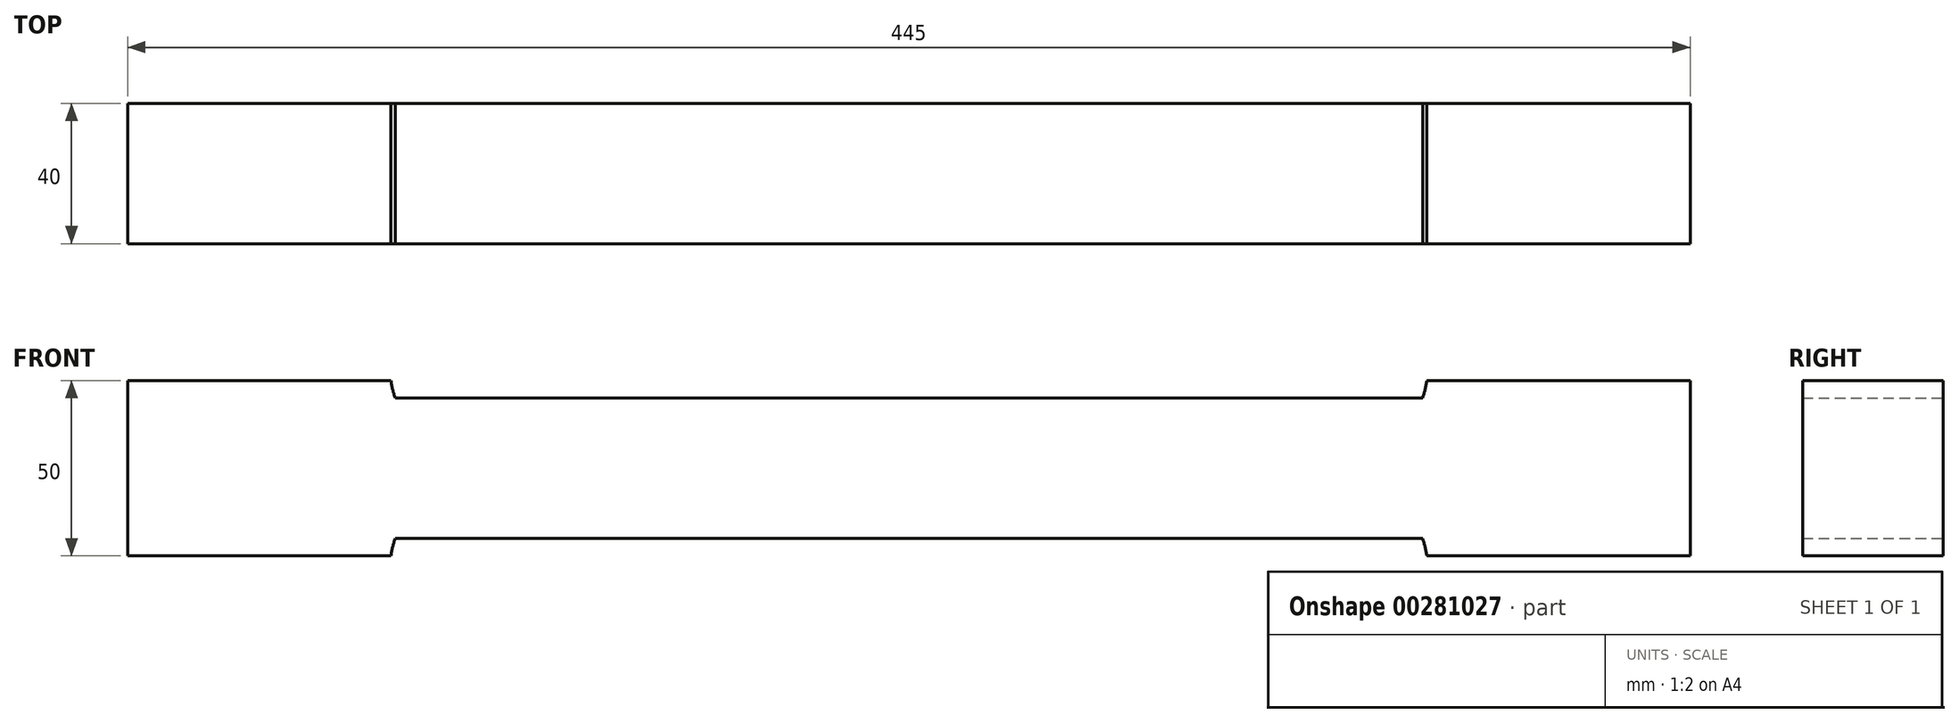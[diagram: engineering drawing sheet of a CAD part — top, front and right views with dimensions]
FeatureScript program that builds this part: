
annotation { "Feature Type Name" : "Feature", "Feature Type Description" : "" }
export const myFeature = defineFeature(function(context is Context, id is Id, definition is map)
    precondition{}
    {
        {
            var Q0;
            Q0=qCreatedBy(makeId("Front.planeOp"),FACE);
            var sketch = newSketch(context, id + "F0", { "sketchPlane" : qUnion([Q0])});
            skLineSegment(sketch, "E0", {"start": v(0, 20) * mm, "end": v(146.3, 20) * mm});
            skArc(sketch, "E1", {"start": v(146.3, 20) * mm, "mid": v(147.03, 22.47) * mm, "end": v(147.5, 25) * mm});
            skLineSegment(sketch, "E2", {"start": v(147.5, 25) * mm, "end": v(222.5, 25) * mm});
            skLineSegment(sketch, "E3", {"start": v(222.5, 25) * mm, "end": v(222.5, 0) * mm});
            skLineSegment(sketch, "E4.MirrorCS", {"start": v(0, -20) * mm, "end": v(146.3, -20) * mm});
            skLineSegment(sketch, "E5.MirrorCS", {"start": v(222.5, -25) * mm, "end": v(222.5, 0) * mm});
            skLineSegment(sketch, "E6.MirrorCS", {"start": v(147.5, -25) * mm, "end": v(222.5, -25) * mm});
            skArc(sketch, "E7.MirrorCS", {"start": v(146.3, -20) * mm, "mid": v(147.03, -22.47) * mm, "end": v(147.5, -25) * mm});
            skLineSegment(sketch, "E8.MirrorCS", {"start": v(0, -20) * mm, "end": v(-146.3, -20) * mm});
            skLineSegment(sketch, "E9.MirrorCS", {"start": v(-222.5, -25) * mm, "end": v(-222.5, 0) * mm});
            skArc(sketch, "E10.MirrorCS", {"start": v(-146.3, -20) * mm, "mid": v(-147.03, -22.47) * mm, "end": v(-147.5, -25) * mm});
            skLineSegment(sketch, "E11.MirrorCS", {"start": v(-147.5, -25) * mm, "end": v(-222.5, -25) * mm});
            skArc(sketch, "E12.MirrorCS", {"start": v(-146.3, 20) * mm, "mid": v(-147.03, 22.47) * mm, "end": v(-147.5, 25) * mm});
            skLineSegment(sketch, "E13.MirrorCS", {"start": v(-147.5, 25) * mm, "end": v(-222.5, 25) * mm});
            skLineSegment(sketch, "E14.MirrorCS", {"start": v(-222.5, 25) * mm, "end": v(-222.5, 0) * mm});
            skLineSegment(sketch, "E15.MirrorCS", {"start": v(0, 20) * mm, "end": v(-146.3, 20) * mm});
            skSolve(sketch);
        }
        {
            var Q0;
            Q0 = qSketchRegion(id + "F0", true);
            extrude(context, id + "F1", {"entities" : qUnion([Q0]), "endBound" : BoundingType.SYMMETRIC, "depth" : 40 * mm});
        }
    });
